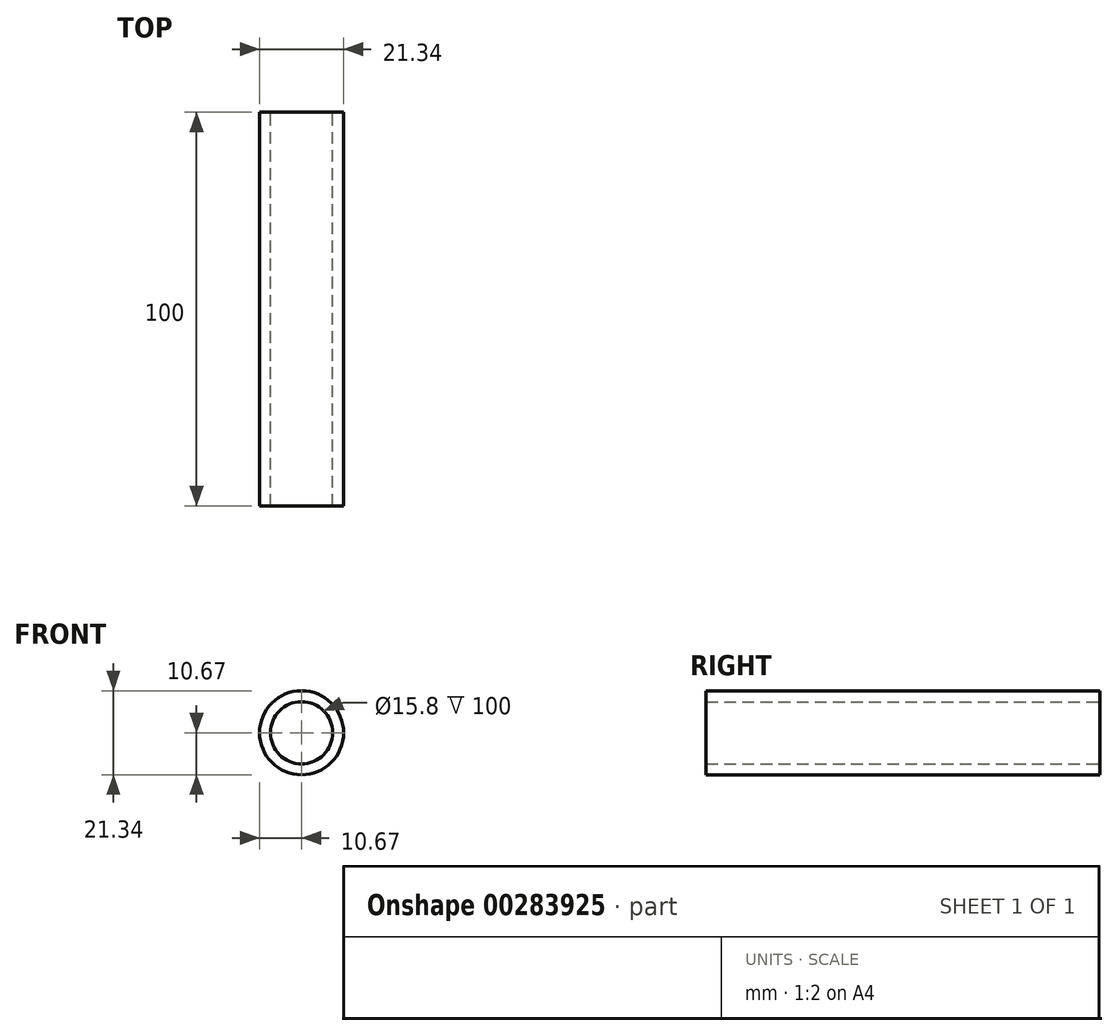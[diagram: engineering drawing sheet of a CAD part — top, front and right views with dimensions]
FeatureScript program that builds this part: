
annotation { "Feature Type Name" : "Feature", "Feature Type Description" : "" }
export const myFeature = defineFeature(function(context is Context, id is Id, definition is map)
    precondition{}
    {
        {
            var Q0;
            Q0=qCreatedBy(makeId("Front.planeOp"),FACE);
            var sketch = newSketch(context, id + "F0", { "sketchPlane" : qUnion([Q0])});
            skCircle(sketch, "E0", {"center": v(0, 0) * mm, "radius": 7.9 * mm});
            skCircle(sketch, "E1", {"center": v(0, 0) * mm, "radius": 10.67 * mm});
            skSolve(sketch);
        }
        {
            var Q0;
            Q0=qSketchRegion(id+"F0",true);
            extrude(context, id + "F1", {"entities" : qUnion([Q0]), "endBound" : BoundingType.SYMMETRIC, "depth" : 100 * mm});
        }
    });
